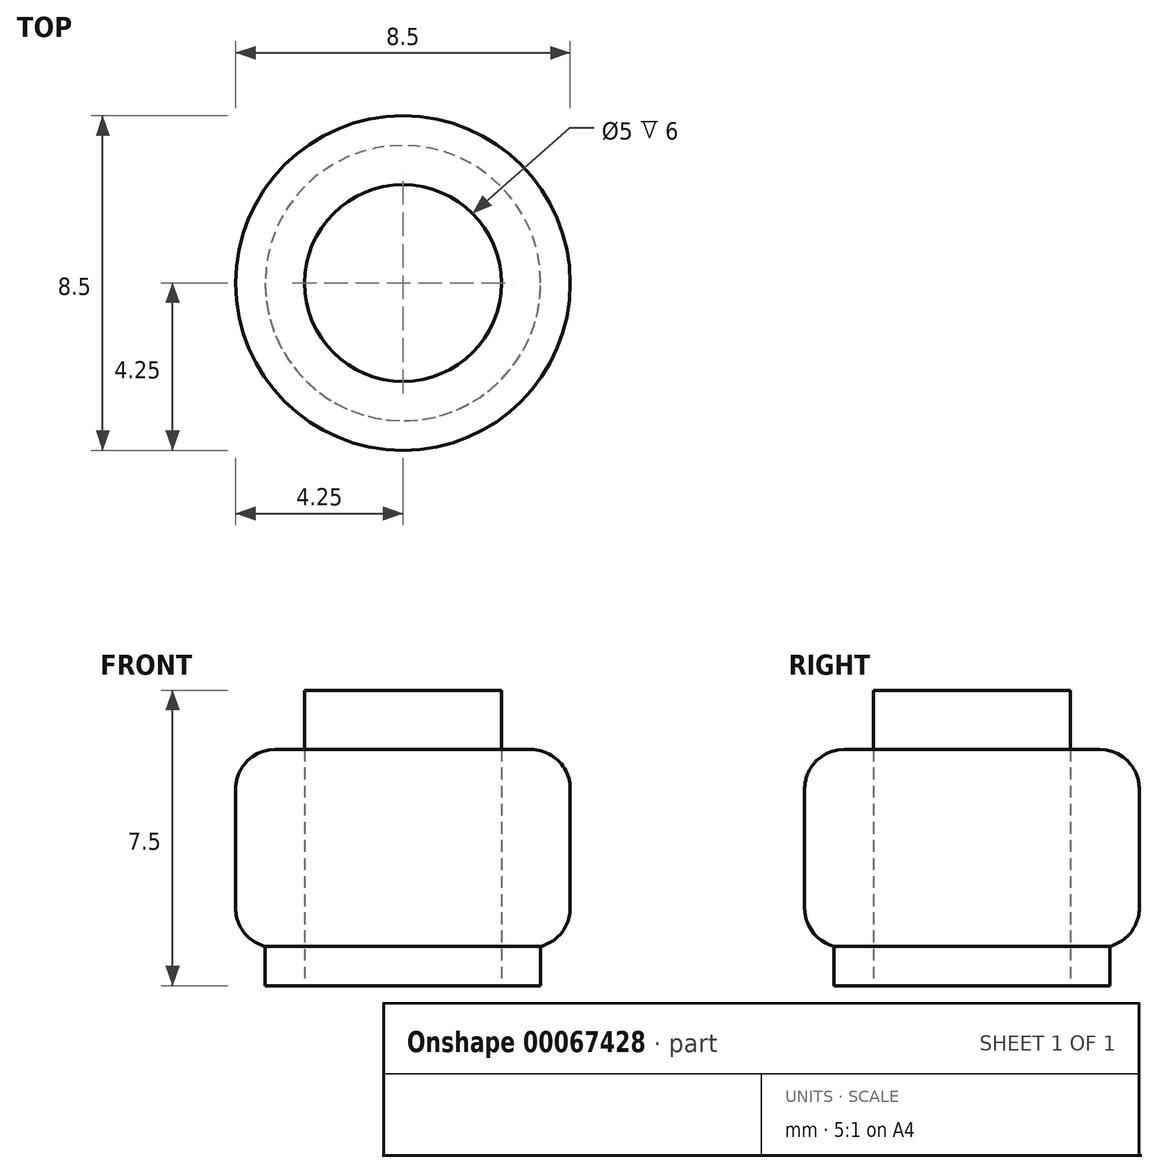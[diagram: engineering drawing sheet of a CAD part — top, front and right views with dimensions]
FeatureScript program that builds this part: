
annotation { "Feature Type Name" : "Feature", "Feature Type Description" : "" }
export const myFeature = defineFeature(function(context is Context, id is Id, definition is map)
    precondition{}
    {
        {
            var Q0;
            Q0=qCreatedBy(makeId("Top.planeOp"),FACE);
            var sketch = newSketch(context, id + "F0", { "sketchPlane" : qUnion([Q0])});
            skCircle(sketch, "E0", {"center": v(0, 0) * mm, "radius": 3.5 * mm});
            skSolve(sketch);
        }
        {
            var Q0;
            Q0 = qSketchRegion(id + "F0", true);
            extrude(context, id + "F1", {"entities" : qUnion([Q0]), "depth" : 1 * mm});
        }
        {
            var Q0;
            Q0=makeQuery(id+"F1.opExtrude","CAP_FACE",FACE,{"disambiguationData":[OSD([sQuery(id+"F0.wireOp",EDGE,"E0")])],"isStart":false});
            var sketch = newSketch(context, id + "F2", { "sketchPlane" : qUnion([Q0])});
            skCircle(sketch, "E1", {"center": v(0, 0) * mm, "radius": 4.25 * mm});
            skSolve(sketch);
        }
        {
            var Q0;
            Q0 = qSketchRegion(id + "F2", true);
            extrude(context, id + "F3", {"entities" : qUnion([Q0]), "operationType" : NewBodyOperationType.ADD, "depth" : 5 * mm});
        }
        {
            var Q0;
            Q0=makeQuery(id+"F3.opExtrude","CAP_FACE",FACE,{"disambiguationData":[OSD([sQuery(id+"F2.wireOp",EDGE,"E1")])],"isStart":false});
            var sketch = newSketch(context, id + "F4", { "sketchPlane" : qUnion([Q0])});
            skCircle(sketch, "E2", {"center": v(0, 0) * mm, "radius": 2.5 * mm});
            skSolve(sketch);
        }
        {
            var Q0;
            Q0 = qSketchRegion(id + "F4", true);
            extrude(context, id + "F5", {"entities" : qUnion([Q0]), "operationType" : NewBodyOperationType.ADD, "depth" : 1.5 * mm});
        }
        {
            var Q0;
            Q0=makeQuery(id+"F3.opExtrude","CAP_EDGE",EDGE,{"disambiguationData":[OSD([sQuery(id+"F2.wireOp",EDGE,"E1")])],"isStart":false});
            var Q1;
            Q1=makeQuery(id+"F3.opExtrude","CAP_EDGE",EDGE,{"disambiguationData":[OSD([sQuery(id+"F2.wireOp",EDGE,"E1")])],"isStart":true});
            fillet(context, id + "F6", {"entities" : qUnion([Q0, Q1]), "radius" : 1 * mm, "tangentPropagation" : true, "allowEdgeOverflow" : false});
        }
        {
            var Q0;
            Q0=makeQuery(id+"F1.opExtrude","CAP_FACE",FACE,{"disambiguationData":[OSD([sQuery(id+"F0.wireOp",EDGE,"E0")])],"isStart":true});
            var sketch = newSketch(context, id + "F7", { "sketchPlane" : qUnion([Q0])});
            skCircle(sketch, "E3", {"center": v(0, 0) * mm, "radius": 2.5 * mm});
            skSolve(sketch);
        }
        {
            var Q0;
            Q0 = qSketchRegion(id + "F7", true);
            extrude(context, id + "F8", {"entities" : qUnion([Q0]), "operationType" : NewBodyOperationType.REMOVE, "oppositeDirection" : true, "depth" : 6 * mm});
        }
    });
